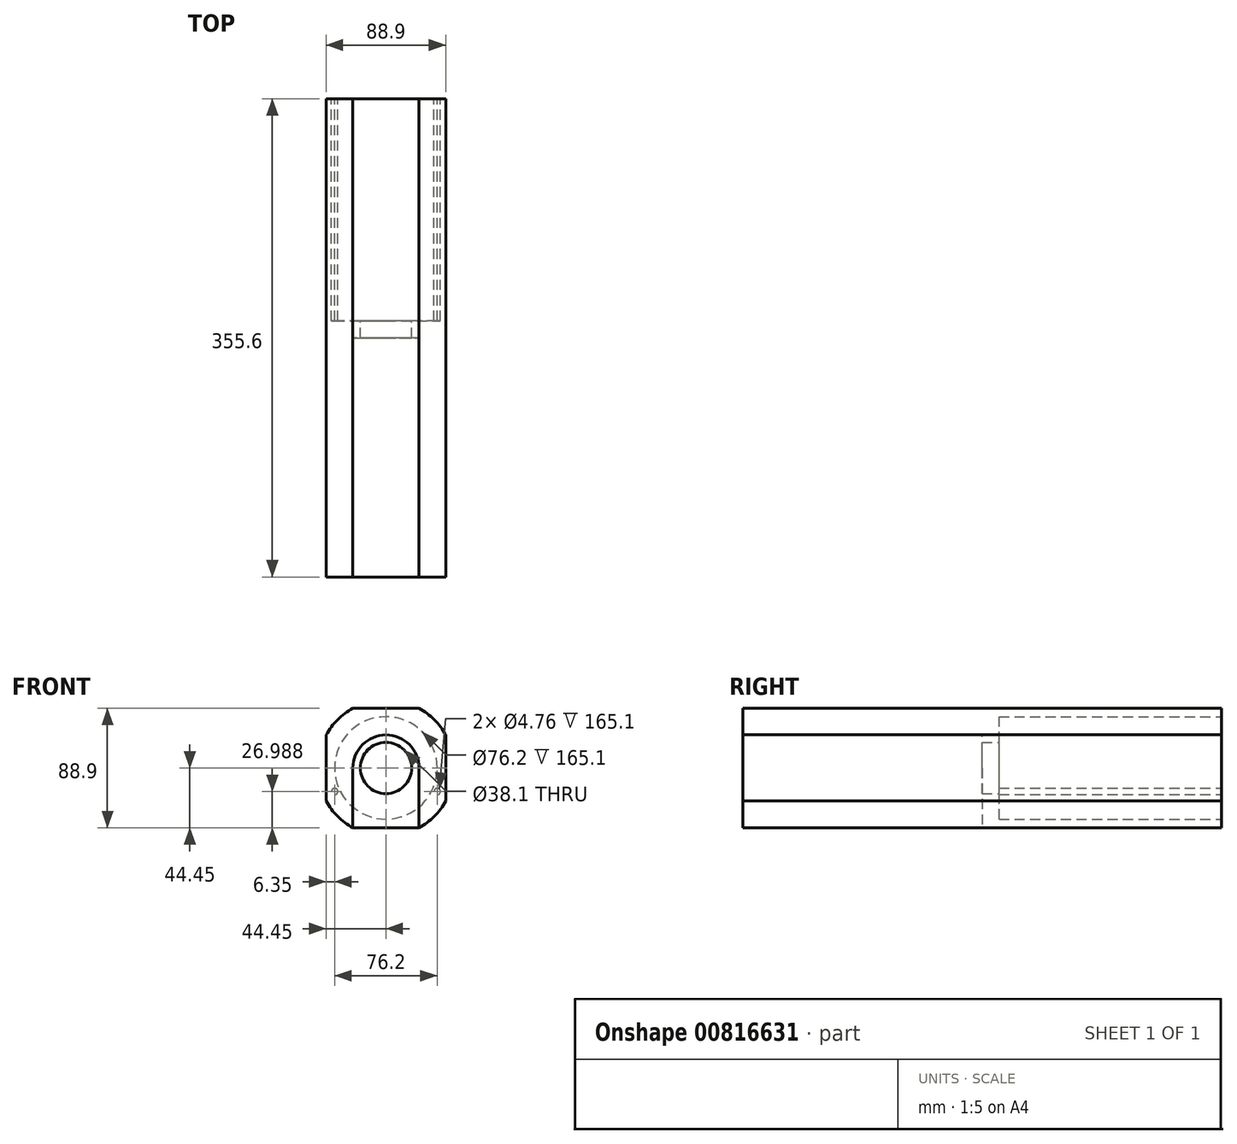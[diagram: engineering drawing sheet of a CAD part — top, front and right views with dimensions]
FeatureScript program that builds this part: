
annotation { "Feature Type Name" : "Feature", "Feature Type Description" : "" }
export const myFeature = defineFeature(function(context is Context, id is Id, definition is map)
    precondition{}
    {
        {
            var Q0;
            Q0=qCreatedBy(makeId("Front.planeOp"),FACE);
            var sketch = newSketch(context, id + "F0", { "sketchPlane" : qUnion([Q0])});
            skLineSegment(sketch, "E0.bottom", {"start": v(-24.6, 44.45) * mm, "end": v(24.6, 44.45) * mm});
            skLineSegment(sketch, "E0.top", {"start": v(-24.6, -44.45) * mm, "end": v(24.6, -44.45) * mm});
            skLineSegment(sketch, "E0.left", {"start": v(-44.45, 24.6) * mm, "end": v(-44.45, -24.6) * mm});
            skLineSegment(sketch, "E0.right", {"start": v(44.45, 24.6) * mm, "end": v(44.45, -24.6) * mm});
            skPoint(sketch, "E0.middle", {"position": v(0, 0) * mm});
            skCircle(sketch, "E1", {"center": v(0, 0) * mm, "radius": 38.1 * mm});
            skArc(sketch, "E2", {"start": v(-24.6, 44.45) * mm, "mid": v(-35.92, 35.92) * mm, "end": v(-44.45, 24.6) * mm});
            skPoint(sketch, "E3.orphan", {"position": v(-44.45, 44.45) * mm});
            skPoint(sketch, "E4.orphan", {"position": v(44.45, 44.45) * mm});
            skArc(sketch, "E5.trimOffspring", {"start": v(44.45, 24.6) * mm, "mid": v(35.92, 35.92) * mm, "end": v(24.6, 44.45) * mm});
            skPoint(sketch, "E6.orphan", {"position": v(44.45, -44.45) * mm});
            skArc(sketch, "E7.trimOffspring", {"start": v(24.6, -44.45) * mm, "mid": v(35.92, -35.92) * mm, "end": v(44.45, -24.6) * mm});
            skPoint(sketch, "E8.orphan", {"position": v(-44.45, -44.45) * mm});
            skArc(sketch, "E9.trimOffspring", {"start": v(-44.45, -24.6) * mm, "mid": v(-35.92, -35.92) * mm, "end": v(-24.6, -44.45) * mm});
            skPoint(sketch, "E10", {"position": v(38.1, -17.46) * mm});
            skCircle(sketch, "E11", {"center": v(38.1, -17.46) * mm, "radius": 2.38 * mm});
            skPoint(sketch, "E12", {"position": v(-38.1, -17.46) * mm});
            skCircle(sketch, "E13", {"center": v(-38.1, -17.46) * mm, "radius": 2.38 * mm});
            skSolve(sketch);
        }
        {
            var Q0;
            Q0 = qSketchRegion(id + "F0", true);
            extrude(context, id + "F1", {"entities" : qUnion([Q0]), "depth" : 165.1 * mm, "offsetDistance" : 25.4 * mm});
        }
        {
            var Q0;
            Q0=makeQuery(id+"F1.opExtrude","CAP_FACE",FACE,{"disambiguationData":[OSD([sQuery(id+"F0.wireOp",EDGE,"E0.bottom"),sQuery(id+"F0.wireOp",EDGE,"E0.top"),sQuery(id+"F0.wireOp",EDGE,"E0.left"),sQuery(id+"F0.wireOp",EDGE,"E0.right"),sQuery(id+"F0.wireOp",EDGE,"E1"),sQuery(id+"F0.wireOp",EDGE,"E2"),sQuery(id+"F0.wireOp",EDGE,"E5.trimOffspring"),sQuery(id+"F0.wireOp",EDGE,"E7.trimOffspring"),sQuery(id+"F0.wireOp",EDGE,"E9.trimOffspring")])],"isStart":false});
            var sketch = newSketch(context, id + "F2", { "sketchPlane" : qUnion([Q0])});
            skLineSegment(sketch, "E14.bottom", {"start": v(-24.6, 44.45) * mm, "end": v(24.6, 44.45) * mm});
            skLineSegment(sketch, "E14.top", {"start": v(-24.6, -44.45) * mm, "end": v(24.6, -44.45) * mm});
            skLineSegment(sketch, "E14.left", {"start": v(-44.45, 24.6) * mm, "end": v(-44.45, -24.6) * mm});
            skLineSegment(sketch, "E14.right", {"start": v(44.45, 24.6) * mm, "end": v(44.45, -24.6) * mm});
            skPoint(sketch, "E14.middle", {"position": v(0, 0) * mm});
            skArc(sketch, "E15", {"start": v(-24.6, 44.45) * mm, "mid": v(-35.92, 35.92) * mm, "end": v(-44.45, 24.6) * mm});
            skCircle(sketch, "E16", {"center": v(0, 0) * mm, "radius": 19.05 * mm});
            skPoint(sketch, "E17.orphan", {"position": v(-44.45, 44.45) * mm});
            skPoint(sketch, "E18.orphan", {"position": v(44.45, 44.45) * mm});
            skArc(sketch, "E19.trimOffspring", {"start": v(44.45, 24.6) * mm, "mid": v(35.92, 35.92) * mm, "end": v(24.6, 44.45) * mm});
            skPoint(sketch, "E20.orphan", {"position": v(44.45, -44.45) * mm});
            skArc(sketch, "E21.trimOffspring", {"start": v(24.6, -44.45) * mm, "mid": v(35.92, -35.92) * mm, "end": v(44.45, -24.6) * mm});
            skPoint(sketch, "E22.orphan", {"position": v(-44.45, -44.45) * mm});
            skArc(sketch, "E23.trimOffspring", {"start": v(-44.45, -24.6) * mm, "mid": v(-35.92, -35.92) * mm, "end": v(-24.6, -44.45) * mm});
            skSolve(sketch);
        }
        {
            var Q0;
            Q0 = qSketchRegion(id + "F2", true);
            extrude(context, id + "F3", {"entities" : qUnion([Q0]), "operationType" : NewBodyOperationType.ADD, "depth" : 12.7 * mm, "offsetDistance" : 25.4 * mm});
        }
        {
            var Q0;
            Q0=makeQuery(id+"F3.opExtrude","CAP_FACE",FACE,{"disambiguationData":[OSD([sQuery(id+"F2.wireOp",EDGE,"E14.bottom"),sQuery(id+"F2.wireOp",EDGE,"E14.top"),sQuery(id+"F2.wireOp",EDGE,"E14.left"),sQuery(id+"F2.wireOp",EDGE,"E14.right"),sQuery(id+"F2.wireOp",EDGE,"E15"),sQuery(id+"F2.wireOp",EDGE,"E16"),sQuery(id+"F2.wireOp",EDGE,"E19.trimOffspring"),sQuery(id+"F2.wireOp",EDGE,"E21.trimOffspring"),sQuery(id+"F2.wireOp",EDGE,"E23.trimOffspring")])],"isStart":false});
            var sketch = newSketch(context, id + "F4", { "sketchPlane" : qUnion([Q0])});
            skLineSegment(sketch, "E24.bottom", {"start": v(-24.6, 44.45) * mm, "end": v(24.6, 44.45) * mm});
            skLineSegment(sketch, "E24.top", {"start": v(-24.6, -44.45) * mm, "end": v(24.6, -44.45) * mm});
            skLineSegment(sketch, "E24.left", {"start": v(-44.45, 24.6) * mm, "end": v(-44.45, -24.6) * mm});
            skLineSegment(sketch, "E24.right", {"start": v(44.45, 24.6) * mm, "end": v(44.45, -24.6) * mm});
            skPoint(sketch, "E24.middle", {"position": v(0, 0) * mm});
            skArc(sketch, "E25", {"start": v(-24.6, 44.45) * mm, "mid": v(-35.92, 35.92) * mm, "end": v(-44.45, 24.6) * mm});
            skPoint(sketch, "E26.orphan", {"position": v(-44.45, 44.45) * mm});
            skPoint(sketch, "E27.orphan", {"position": v(44.45, 44.45) * mm});
            skArc(sketch, "E28.trimOffspring", {"start": v(44.45, 24.6) * mm, "mid": v(35.92, 35.92) * mm, "end": v(24.6, 44.45) * mm});
            skPoint(sketch, "E29.orphan", {"position": v(44.45, -44.45) * mm});
            skArc(sketch, "E30.trimOffspring", {"start": v(24.6, -44.45) * mm, "mid": v(35.92, -35.92) * mm, "end": v(44.45, -24.6) * mm});
            skPoint(sketch, "E31.orphan", {"position": v(-44.45, -44.45) * mm});
            skArc(sketch, "E32.trimOffspring", {"start": v(-44.45, -24.6) * mm, "mid": v(-35.92, -35.92) * mm, "end": v(-24.6, -44.45) * mm});
            skCircle(sketch, "E33", {"center": v(0, 0) * mm, "radius": 24.59 * mm});
            skLineSegment(sketch, "E34", {"start": v(-24.59, 0) * mm, "end": v(-24.6, -44.45) * mm});
            skLineSegment(sketch, "E35", {"start": v(24.59, 0) * mm, "end": v(24.6, -44.45) * mm});
            skSolve(sketch);
        }
        {
            var Q0;
            Q0=makeQuery(id+"F4.imprint","IMPRINT",FACE,{"disambiguationData":[TD([[makeQuery(id+"F4.imprint","IMPRINT",EDGE,{"derivedFrom":sQuery(id+"F4.wireOp",EDGE,"E24.bottom")}),-1.0]])]});
            extrude(context, id + "F5", {"entities" : qUnion([Q0]), "operationType" : NewBodyOperationType.ADD, "depth" : 177.8 * mm, "offsetDistance" : 25.4 * mm});
        }
    });
